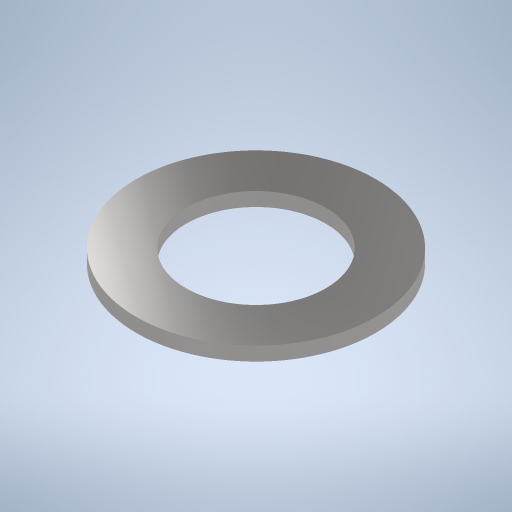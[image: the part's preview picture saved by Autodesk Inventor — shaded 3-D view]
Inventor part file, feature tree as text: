
AUTODESK INVENTOR PART (.ipt)
format: ipt  version: 2023 (Build 270158000, 158)  size: 246,784 bytes
history: native  units: mm
features: extrude x1, sketch x1
ambient origin geometry x8: Origin, YZ Plane, XZ Plane, XY Plane, X Axis, Y Axis, Z Axis, Center Point
bodies: Volumenkörper1 (feature_tree)
feature tree (2):
  extrude  "Extrusion1"  Depth=2.0mm
  sketch  "Skizze1"  dims[d0=20.15mm d1=34.5mm d2=2.0mm d3=0.0mm]
